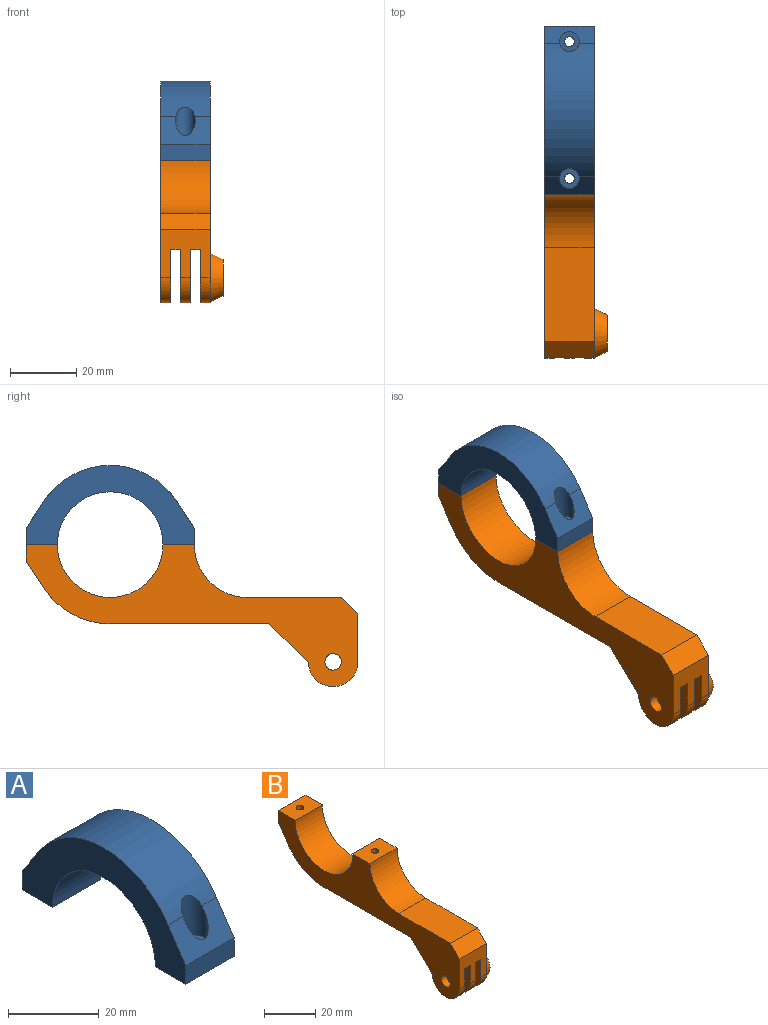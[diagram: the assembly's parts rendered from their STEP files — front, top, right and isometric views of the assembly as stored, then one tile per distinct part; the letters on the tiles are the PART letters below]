
ASSEMBLY  parts=2 mates=1
PART A: 16 faces, bbox 15x51x24 mm
  f0: cylinder r=24mm len=40.02mm, axis (-1,0,0), area 677.4mm2, adj f6,f7,f10,f11,f12,f14
  f1: cylinder r=1.5mm len=5mm, axis (0,0,-1), area 47.1mm2, adj f9,f15
  f2: cylinder r=1.5mm len=5mm, axis (0,0,-1), area 47.1mm2, adj f4,f13
  f3: cylinder r=16mm len=32mm, axis (-1,0,0), area 754mm2, adj f4,f9,f10,f11
  f4: plane 15x9.47mm, normal (0,0,-1), area 135mm2, adj f2,f3,f5,f10,f11
  f5: plane 15x5mm, normal (0,1,0), area 75mm2, adj f4,f6,f10,f11
  f6: plane 15.01x8.26mm, normal (0,0.83,0.55), area 115mm2, adj f0,f5,f10,f11,f12
  f7: plane 15.01x8.26mm, normal (0,-0.83,0.55), area 115mm2, adj f0,f8,f10,f11,f14
  f8: plane 15x5mm, normal (0,-1,0), area 75mm2, adj f7,f9,f10,f11
  f9: plane 15x9.47mm, normal (0,0,-1), area 135mm2, adj f1,f3,f8,f10,f11
  f10: plane 50.95x24mm, normal (1,0,0), area 530.6mm2, adj f0,f3,f4,f5,f6,f7,f8,f9
  f11: plane 50.95x24mm, normal (-1,0,0), area 530.6mm2, adj f0,f3,f4,f5,f6,f7,f8,f9
  f12: cylinder r=3mm len=11.17mm, axis (0,0,-1), area 132.7mm2, adj f0,f6,f13
  f13: plane 6x6mm, normal (0,0,1), area 21.2mm2, adj f2,f12
  f14: cylinder r=3mm len=11.17mm, axis (0,0,-1), area 132.7mm2, adj f0,f7,f15
  f15: plane 6x6mm, normal (0,0,1), area 21.2mm2, adj f1,f14
PART B: 51 faces, bbox 19x100.5x43 mm
  f0: cylinder r=24mm len=20.01mm, axis (-1,0,0), area 336.4mm2, adj f1,f8,f10,f11,f35,f36,f37
  f1: plane 15x8.25mm, normal (0,0.83,-0.55), area 110.5mm2, adj f0,f9,f10,f11,f36,f37,f38,f39
  f2: plane 15x9.47mm, normal (0,0,1), area 135mm2, adj f3,f9,f10,f11,f34
  f3: cylinder r=16mm len=32mm, axis (-1,0,0), area 754mm2, adj f2,f4,f10,f11
  f4: plane 15x9.47mm, normal (0,0,1), area 135mm2, adj f3,f5,f10,f11,f42
  f5: cylinder r=16mm len=16mm, axis (-1,0,0), area 377mm2, adj f4,f6,f10,f11
  f6: plane 28.53x15mm, normal (0,0,1), area 427.9mm2, adj f5,f10,f11,f32
  f7: plane 15x14.5mm, normal (0,-1,0), area 166.5mm2, adj f10,f11,f13,f14,f15,f16,f17,f18
  f8: plane 48.01x15mm, normal (0,0,-1), area 687.9mm2, adj f0,f10,f11,f33,f43,f44,f45,f46
  f9: plane 15x5mm, normal (0,1,0), area 75mm2, adj f1,f2,f10,f11
  f10: plane 100.47x35.69mm, normal (1,0,0), area 1268.5mm2, adj f0,f1,f2,f3,f4,f5,f6,f7
  f11: plane 100.47x43mm, normal (-1,0,0), area 1425.6mm2, adj f0,f1,f2,f3,f4,f5,f6,f7
  f12: plane 9.24x8mm, normal (1,0,0), area 35.8mm2, adj f24,f25,f26,f27,f28,f29,f30
  f13: plane 23.92x3mm, normal (0,0,-1), area 71.7mm2, adj f7,f17,f18,f33
  f14: plane 23.92x3mm, normal (0,0,-1), area 71.7mm2, adj f7,f15,f16,f33
  f15: plane 23.92x16mm, normal (-1,0,0), area 235mm2, adj f7,f14,f21,f24,f33
  f16: plane 23.92x16mm, normal (1,0,0), area 235mm2, adj f7,f14,f20,f23,f33
  f17: plane 23.92x16mm, normal (-1,0,0), area 235mm2, adj f7,f13,f20,f23,f33
  f18: plane 23.92x16mm, normal (1,0,0), area 235mm2, adj f7,f13,f19,f22,f33
  f19: cylinder r=7.5mm len=15mm, axis (1,0,0), area 70.1mm2, adj f7,f11,f18,f33
  f20: cylinder r=7.5mm len=15mm, axis (1,0,0), area 70.1mm2, adj f7,f16,f17,f33
  f21: cylinder r=7.5mm len=15mm, axis (-1,0,0), area 70.1mm2, adj f7,f15,f33,f50
  f22: cylinder r=2.5mm len=5mm, axis (1,0,0), area 47.1mm2, adj f11,f18
  f23: cylinder r=2.5mm len=5mm, axis (1,0,0), area 47.1mm2, adj f16,f17
  f24: cylinder r=2.5mm len=5mm, axis (1,0,0), area 47.1mm2, adj f12,f15
  f25: plane 4x4mm, normal (0,-0.87,-0.5), area 18.5mm2, adj f12,f26,f30,f31
  f26: plane 4x4mm, normal (0,-0.87,0.5), area 18.5mm2, adj f12,f25,f27,f31
  f27: plane 4.62x4mm, normal (0,0,1), area 18.5mm2, adj f12,f26,f28,f31
  f28: plane 4x4mm, normal (0,0.87,0.5), area 18.5mm2, adj f12,f27,f29,f31
  f29: plane 4x4mm, normal (0,0.87,-0.5), area 18.5mm2, adj f12,f28,f30,f31
  f30: plane 4.62x4mm, normal (0,0,-1), area 18.5mm2, adj f12,f25,f29,f31
  f31: plane 11x11mm, normal (1,0,0), area 39.6mm2, adj f25,f26,f27,f28,f29,f30,f50
  f32: plane 15x5mm, normal (0,-0.71,0.71), area 106.1mm2, adj f6,f7,f10,f11
  f33: plane 15x12mm, normal (0,0.7,-0.72), area 176.6mm2, adj f8,f10,f11,f13,f14,f15,f16,f17
  f34: cylinder r=1.5mm len=5mm, axis (0,0,1), area 47.1mm2, adj f2,f41
  f35: plane 11.22x3.52mm, normal (0,1,0), area 39.5mm2, adj f0,f36,f37,f41
  f36: plane 11.22x3.05mm, normal (0.87,0.5,0), area 32.8mm2, adj f0,f1,f35,f38,f41
  f37: plane 11.22x3.05mm, normal (-0.87,0.5,0), area 32.8mm2, adj f0,f1,f35,f39,f41
  f38: plane 7.15x3.05mm, normal (0.87,-0.5,0), area 17.1mm2, adj f1,f36,f40,f41
  f39: plane 7.15x3.05mm, normal (-0.87,-0.5,0), area 17.1mm2, adj f1,f37,f40,f41
  f40: plane 3.52x2.55mm, normal (0,-1,0), area 9mm2, adj f1,f38,f39,f41
  f41: plane 7.04x6.1mm, normal (0,0,-1), area 25.2mm2, adj f34,f35,f36,f37,f38,f39,f40
  f42: cylinder r=1.5mm len=5mm, axis (0,0,1), area 47.1mm2, adj f4,f49
  f43: plane 19x3.05mm, normal (0.87,0.5,0), area 66.9mm2, adj f8,f44,f48,f49
  f44: plane 19x3.52mm, normal (0,1,0), area 66.9mm2, adj f8,f43,f45,f49
  f45: plane 19x3.05mm, normal (-0.87,0.5,0), area 66.9mm2, adj f8,f44,f46,f49
  f46: plane 19x3.05mm, normal (-0.87,-0.5,0), area 66.9mm2, adj f8,f45,f47,f49
  f47: plane 19x3.52mm, normal (0,-1,0), area 66.9mm2, adj f8,f46,f48,f49
  f48: plane 19x3.05mm, normal (0.87,-0.5,0), area 66.9mm2, adj f8,f43,f47,f49
  f49: plane 7.04x6.1mm, normal (0,0,-1), area 25.2mm2, adj f42,f43,f44,f45,f46,f47,f48
  f50: cone r=5mm half-angle=26.6deg, axis (-1,0,0), area 182.6mm2, adj f10,f21,f31
PLACE A t=(-44.35,-18.71,-0.92)mm
PLACE B t=(-44.35,-18.71,-0.92)mm
MATE fastened A.f4 <-> B.f2  axis (0,0,-1) through (-44.35,6.76,-0.92)mm
